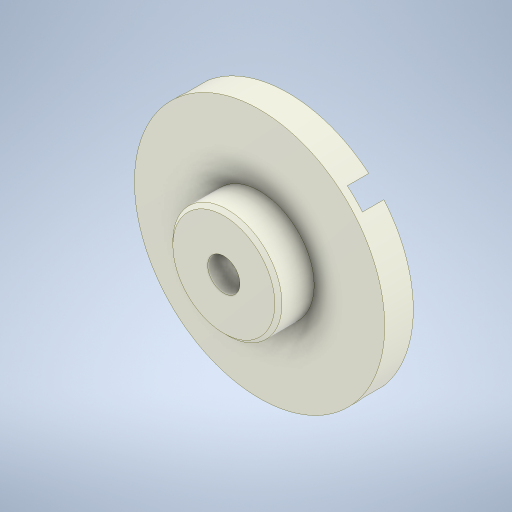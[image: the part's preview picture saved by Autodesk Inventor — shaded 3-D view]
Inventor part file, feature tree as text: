
AUTODESK INVENTOR PART (.ipt)
format: ipt  version: 2023.1 (Build 271208000, 208)  size: 342,528 bytes
history: native  units: mm
features: extrude x7, sketch x7, chamfer x3, pattern_circular x2, plane x1, fillet x1
ambient origin geometry x8: Origin, YZ Plane, XZ Plane, XY Plane, X Axis, Y Axis, Z Axis, Center Point
bodies: Solid1 (feature_tree)
feature tree (21):
  extrude  "Extrusion1"  Depth=4.0mm TaperAngle=0.0deg
  extrude  "Extrusion2"  Depth=5.0mm TaperAngle=0.0deg
  chamfer  "Chamfer1"  Distance=2.0mm Angle=45.0deg
  extrude  "Extrusion3"  Depth=1.2mm TaperAngle=0.0deg
  extrude  "Extrusion4"  Depth=3.0mm TaperAngle=0.0deg
  extrude  "Extrusion5"  TaperAngle=45.0deg  [1 undecoded]
  pattern_circular  "Circular Pattern1"  Count=4 Angle=360.0deg
  extrude  "Extrusion6"  TaperAngle=0.0deg  [1 undecoded]
  plane  "Work Plane1"
  extrude  "Extrusion7"  TaperAngle=45.0deg  [1 undecoded]
  pattern_circular  "Circular Pattern2"  [2 undecoded]
  chamfer  "Chamfer2"  Distance=2.0mm
  fillet  "Fillet1"  Radius=40.0mm
  chamfer  "Chamfer3"  Distance=2.0mm Angle=45.0deg
  sketch  "Sketch1"  dims[d0=35.0mm d1=4.0mm d2=0.0mm]
  sketch  "Sketch2"  dims[d3=15.25mm d4=5.0mm d5=0.0mm d6=0.5mm d7=2.0mm d8=45.0deg]
  sketch  "Sketch3"  dims[d9=14.8mm d10=1.2mm d11=0.0mm]
  sketch  "Sketch4"  dims[d12=6.0mm d13=3.0mm d14=0.0mm]
  sketch  "Sketch5"  dims[d15=1.5mm d16=45.0deg]
  sketch  "Sketch6"  dims[d17=3.0mm d18=0.0mm d19=40.0mm d20=360.0deg]
  sketch  "Sketch7"  dims[d22=4.5mm d23=0.0mm d24=0.0mm d25=45.0deg d26=2.0mm d27=2.0mm d28=0.0mm d29=40.0mm d30=360.0deg d32=0.5mm d33=2.0mm d34=45.0deg d35=0.4mm d36=0.5mm d37=2.0mm d38=45.0deg]
note: 5 required parameter values undecoded (feature->parameter linkage not recoverable at this tier; creation-order binding heuristic only, values carry confidence <= 0.55)
